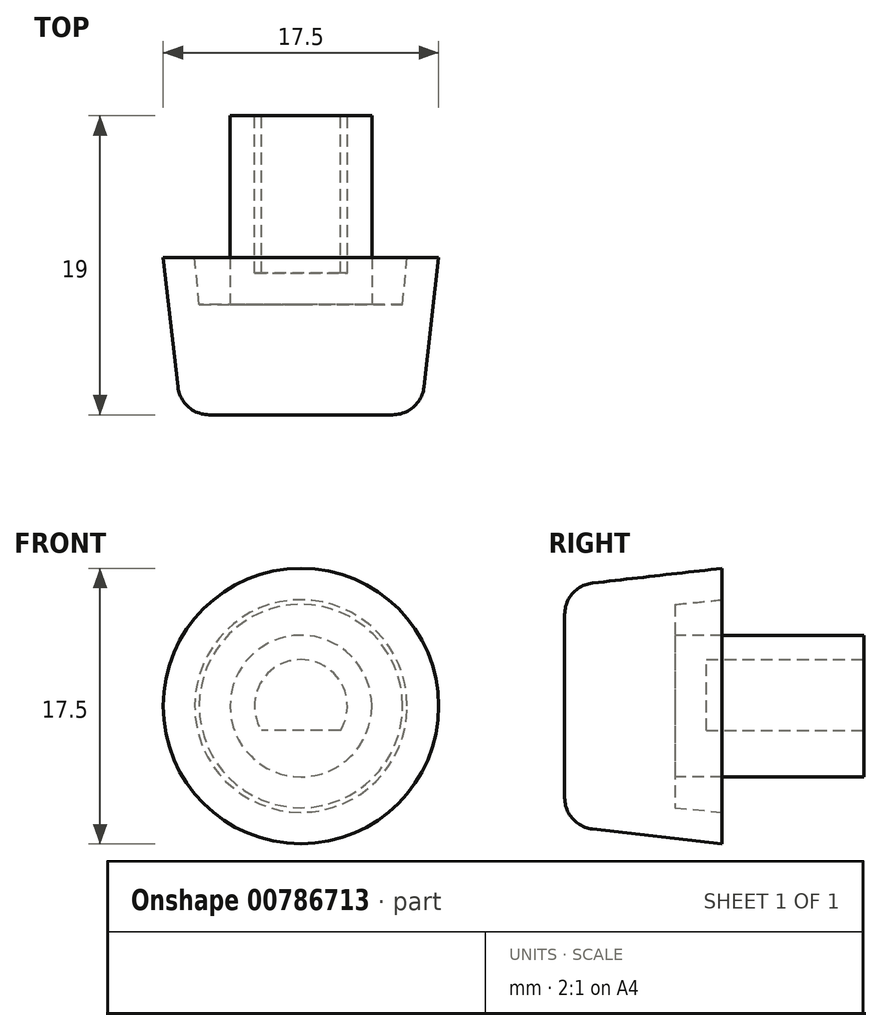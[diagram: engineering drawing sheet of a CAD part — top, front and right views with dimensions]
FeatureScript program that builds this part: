
annotation { "Feature Type Name" : "Feature", "Feature Type Description" : "" }
export const myFeature = defineFeature(function(context is Context, id is Id, definition is map)
    precondition{}
    {
        {
            var Q0;
            Q0=qCreatedBy(makeId("Top.planeOp"),FACE);
            var sketch = newSketch(context, id + "F0", { "sketchPlane" : qUnion([Q0])});
            skLineSegment(sketch, "E0.bottom", {"start": v(0, 0) * mm, "end": v(-8.75, 0) * mm});
            skLineSegment(sketch, "E0.top", {"start": v(0, -10) * mm, "end": v(-5.83, -10) * mm});
            skLineSegment(sketch, "E0.left", {"start": v(0, 0) * mm, "end": v(0, -10) * mm});
            skLineSegment(sketch, "E0.right", {"start": v(-8.75, 0) * mm, "end": v(-7.82, -8.23) * mm});
            skPoint(sketch, "E1.visualSharp", {"position": v(-7.61, -10) * mm});
            skArc(sketch, "E1.filletArc", {"start": v(-7.82, -8.23) * mm, "mid": v(-7.16, -9.5) * mm, "end": v(-5.83, -10) * mm});
            skLineSegment(sketch, "E2.bottom", {"start": v(0, 0) * mm, "end": v(-6.75, 0) * mm});
            skLineSegment(sketch, "E2.top", {"start": v(0, -3) * mm, "end": v(-6.46, -3) * mm});
            skLineSegment(sketch, "E2.left", {"start": v(0, 0) * mm, "end": v(0, -3) * mm});
            skLineSegment(sketch, "E2.right", {"start": v(-6.75, 0) * mm, "end": v(-6.46, -3) * mm});
            skSolve(sketch);
        }
        {
            var Q0;
            {var subQ2=sQuery(id+"F0.wireOp",EDGE,"E0.top");Q0=makeQuery(id+"F0.imprint","IMPRINT",FACE,{"disambiguationData":[TD([[makeQuery(id+"F0.imprint","IMPRINT",EDGE,{"derivedFrom":subQ2}),-1.0]])]});}
            var Q1;
            Q1=sQuery(id+"F0.wireOp",EDGE,"E0.left");
            revolve(context, id + "F1", {"surfaceOperationType" : NewSurfaceOperationType.NEW, "entities" : qUnion([Q0]), "axis" : qUnion([Q1]), "revolveType" : RevolveType.FULL});
        }
        {
            var Q0;
            Q0=makeQuery(id+"F1.opRevolve","SWEPT_FACE",FACE,{"disambiguationData":[OSD([sQuery(id+"F0.wireOp",EDGE,"E2.top")])]});
            var sketch = newSketch(context, id + "F2", { "sketchPlane" : qUnion([Q0])});
            skPoint(sketch, "E3.0", {"position": v(0, 0) * mm});
            skCircle(sketch, "E4", {"center": v(0, 0) * mm, "radius": 4.5 * mm});
            skSolve(sketch);
        }
        {
            var Q0;
            Q0=makeQuery(id+"F2.imprint","IMPRINT",FACE,{"disambiguationData":[TD([[makeQuery(id+"F2.imprint","IMPRINT",EDGE,{"derivedFrom":sQuery(id+"F2.wireOp",EDGE,"E4")}),1.0]])]});
            var Q1;
            Q1=sQuery(id+"F2.wireOp",EDGE,"E4");
            extrude(context, id + "F3", {"entities" : qUnion([Q0]), "operationType" : NewBodyOperationType.ADD, "surfaceEntities" : qUnion([Q1]), "depth" : 12 * mm, "offsetDistance" : 25 * mm});
        }
        {
            var Q0;
            Q0=makeQuery(id+"F3.opExtrude","CAP_FACE",FACE,{"disambiguationData":[OSD([sQuery(id+"F2.wireOp",EDGE,"E4")])],"isStart":false});
            var sketch = newSketch(context, id + "F4", { "sketchPlane" : qUnion([Q0])});
            skArc(sketch, "E5", {"start": v(2.5, -1.55) * mm, "mid": v(0, 2.95) * mm, "end": v(-2.5, -1.55) * mm});
            skLineSegment(sketch, "E6", {"start": v(-2.5, -1.55) * mm, "end": v(2.5, -1.55) * mm});
            skSolve(sketch);
        }
        {
            var Q0;
            Q0 = qSketchRegion(id + "F4", true);
            extrude(context, id + "F5", {"entities" : qUnion([Q0]), "operationType" : NewBodyOperationType.REMOVE, "oppositeDirection" : true, "depth" : 10 * mm, "offsetDistance" : 25 * mm});
        }
    });
